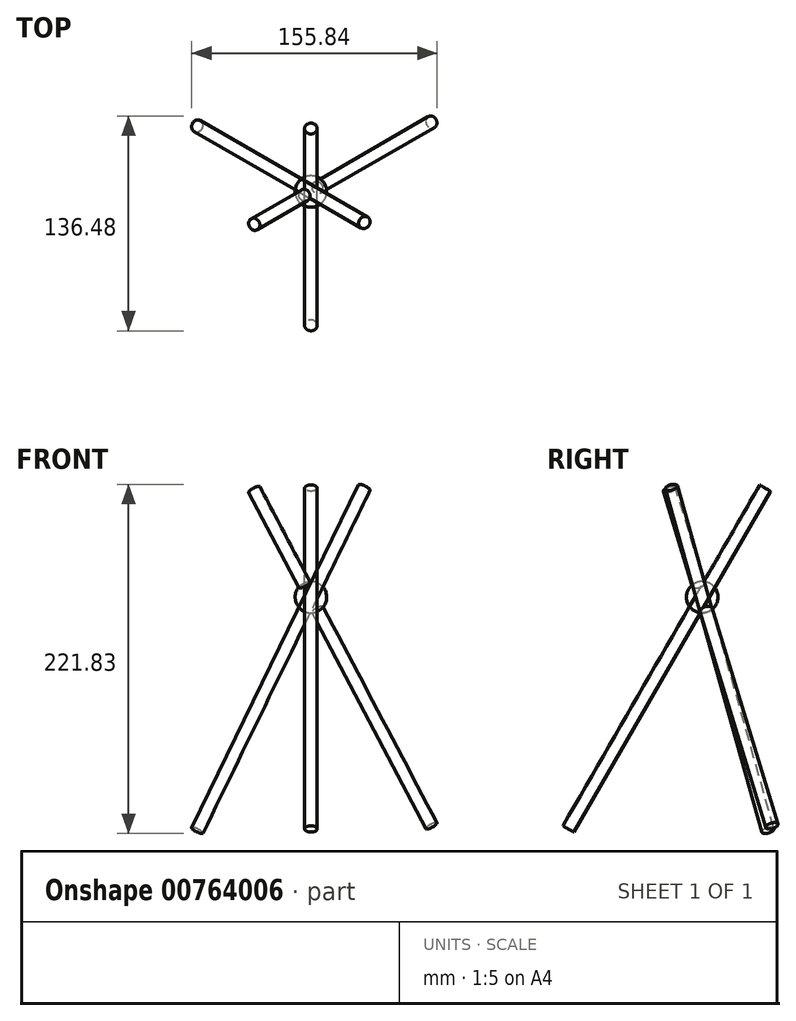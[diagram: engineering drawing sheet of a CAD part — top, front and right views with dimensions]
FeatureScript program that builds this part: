
annotation { "Feature Type Name" : "Feature", "Feature Type Description" : "" }
export const myFeature = defineFeature(function(context is Context, id is Id, definition is map)
    precondition{}
    {
        {
            var Q0;
            Q0=qCreatedBy(makeId("Front.planeOp"),FACE);
            var sketch = newSketch(context, id + "F0", { "sketchPlane" : qUnion([Q0])});
            skArc(sketch, "E0", {"start": v(0, 10) * mm, "mid": v(-10, 0) * mm, "end": v(0, -10) * mm});
            skLineSegment(sketch, "E1", {"start": v(0, -10) * mm, "end": v(0, 0) * mm});
            skLineSegment(sketch, "E2", {"start": v(0, 0) * mm, "end": v(0, 10) * mm});
            skSolve(sketch);
        }
        {
            var Q0;
            Q0=makeQuery(id+"F0.imprint","IMPRINT",FACE,{"disambiguationData":[TD([[makeQuery(id+"F0.imprint","IMPRINT",EDGE,{"derivedFrom":sQuery(id+"F0.wireOp",EDGE,"E0")}),1.0]])]});
            var Q1;
            Q1=sQuery(id+"F0.wireOp",EDGE,"E2");
            revolve(context, id + "F1", {"surfaceOperationType" : NewSurfaceOperationType.NEW, "entities" : qUnion([Q0]), "axis" : qUnion([Q1]), "revolveType" : RevolveType.FULL});
        }
        {
            var Q0;
            Q0=qCreatedBy(makeId("Top.planeOp"),FACE);
            var sketch = newSketch(context, id + "F2", { "sketchPlane" : qUnion([Q0])});
            skCircle(sketch, "E3", {"center": v(0, 0) * mm, "radius": 10 * mm});
            skLineSegment(sketch, "E4", {"start": v(0, 0) * mm, "end": v(0, 74.45) * mm});
            skLineSegment(sketch, "E5", {"start": v(0, 0) * mm, "end": v(-116.73, -67.4) * mm});
            skLineSegment(sketch, "E6", {"start": v(0, 0) * mm, "end": v(102.13, -58.97) * mm});
            skSolve(sketch);
        }
        {
            var Q0;
            Q0=qCreatedBy(makeId("Right.planeOp"),FACE);
            var sketch = newSketch(context, id + "F3", { "sketchPlane" : qUnion([Q0])});
            skLineSegment(sketch, "E7", {"start": v(0, 0) * mm, "end": v(40, 69.28) * mm});
            skSolve(sketch);
        }
        {
            var Q0;
            Q0=sQuery(id+"F2.wireOp",EDGE,"E5");
            cPlane(context, id + "F4", {"entities" : qUnion([Q0]), "cplaneType" : CPlaneType.LINE_ANGLE, "offset" : 25.4 * mm, "angle" : 0 * degree, "width" : 152.4 * mm, "height" : 152.4 * mm});
        }
        {
            var Q0;
            Q0=sQuery(id+"F2.wireOp",EDGE,"E6");
            cPlane(context, id + "F5", {"entities" : qUnion([Q0]), "cplaneType" : CPlaneType.LINE_ANGLE, "offset" : 25.4 * mm, "angle" : 0 * degree, "width" : 152.4 * mm, "height" : 152.4 * mm});
        }
        {
            var Q0;
            Q0=qCreatedBy(id+"F4.planeOp",FACE);
            var sketch = newSketch(context, id + "F6", { "sketchPlane" : qUnion([Q0])});
            skLineSegment(sketch, "E8", {"start": v(0, 0) * mm, "end": v(-41.56, 68.36) * mm});
            skLineSegment(sketch, "E9", {"start": v(0, 0) * mm, "end": v(-4.76, 209.91) * mm, "construction": true});
            skSolve(sketch);
        }
        {
            var Q0;
            Q0=qCreatedBy(id+"F5.planeOp",FACE);
            var sketch = newSketch(context, id + "F7", { "sketchPlane" : qUnion([Q0])});
            skLineSegment(sketch, "E10", {"start": v(0, 0) * mm, "end": v(-39.21, 69.73) * mm});
            skSolve(sketch);
        }
        {
            var Q0;
            Q0=sQuery(id+"F6.wireOp",VERTEX,"E8.end");
            var Q1;
            Q1=sQuery(id+"F6.wireOp",EDGE,"E8");
            cPlane(context, id + "F8", {"entities" : qUnion([Q0, Q1]), "cplaneType" : CPlaneType.LINE_POINT, "offset" : 25.4 * mm, "width" : 152.4 * mm, "height" : 152.4 * mm});
        }
        {
            var Q0;
            Q0=sQuery(id+"F3.wireOp",VERTEX,"E7.end");
            var Q1;
            Q1=sQuery(id+"F3.wireOp",EDGE,"E7");
            cPlane(context, id + "F9", {"entities" : qUnion([Q0, Q1]), "cplaneType" : CPlaneType.LINE_POINT, "offset" : 25.4 * mm, "width" : 152.4 * mm, "height" : 152.4 * mm});
        }
        {
            var Q0;
            Q0=sQuery(id+"F7.wireOp",VERTEX,"E10.end");
            var Q1;
            Q1=sQuery(id+"F7.wireOp",EDGE,"E10");
            cPlane(context, id + "F10", {"entities" : qUnion([Q0, Q1]), "cplaneType" : CPlaneType.LINE_POINT, "offset" : 25.4 * mm, "width" : 152.4 * mm, "height" : 152.4 * mm});
        }
        {
            var Q0;
            Q0=qCreatedBy(id+"F9.planeOp",FACE);
            var sketch = newSketch(context, id + "F11", { "sketchPlane" : qUnion([Q0])});
            skCircle(sketch, "E11", {"center": v(0, 0) * mm, "radius": 4 * mm});
            skSolve(sketch);
        }
        {
            var Q0;
            Q0=qCreatedBy(id+"F8.planeOp",FACE);
            var sketch = newSketch(context, id + "F12", { "sketchPlane" : qUnion([Q0])});
            skCircle(sketch, "E12", {"center": v(0, 0) * mm, "radius": 4 * mm});
            skSolve(sketch);
        }
        {
            var Q0;
            Q0=qCreatedBy(id+"F10.planeOp",FACE);
            var sketch = newSketch(context, id + "F13", { "sketchPlane" : qUnion([Q0])});
            skCircle(sketch, "E13", {"center": v(0, 0) * mm, "radius": 4 * mm});
            skSolve(sketch);
        }
        {
            var Q0;
            Q0=makeQuery(id+"F12.imprint","IMPRINT",FACE,{"disambiguationData":[TD([[makeQuery(id+"F12.imprint","IMPRINT",EDGE,{"derivedFrom":sQuery(id+"F12.wireOp",EDGE,"E12")}),1.0]])]});
            extrude(context, id + "F14", {"entities" : qUnion([Q0]), "operationType" : NewBodyOperationType.ADD, "oppositeDirection" : true, "depth" : 250 * mm, "offsetDistance" : 25 * mm});
        }
        {
            var Q0;
            Q0=makeQuery(id+"F11.imprint","IMPRINT",FACE,{"disambiguationData":[TD([[makeQuery(id+"F11.imprint","IMPRINT",EDGE,{"derivedFrom":sQuery(id+"F11.wireOp",EDGE,"E11")}),1.0]])]});
            extrude(context, id + "F15", {"entities" : qUnion([Q0]), "oppositeDirection" : true, "depth" : 250 * mm, "offsetDistance" : 25 * mm});
        }
        {
            var Q0;
            Q0=makeQuery(id+"F13.imprint","IMPRINT",FACE,{"disambiguationData":[TD([[makeQuery(id+"F13.imprint","IMPRINT",EDGE,{"derivedFrom":sQuery(id+"F13.wireOp",EDGE,"E13")}),1.0]])]});
            extrude(context, id + "F16", {"entities" : qUnion([Q0]), "oppositeDirection" : true, "depth" : 250 * mm, "offsetDistance" : 25 * mm});
        }
    });
